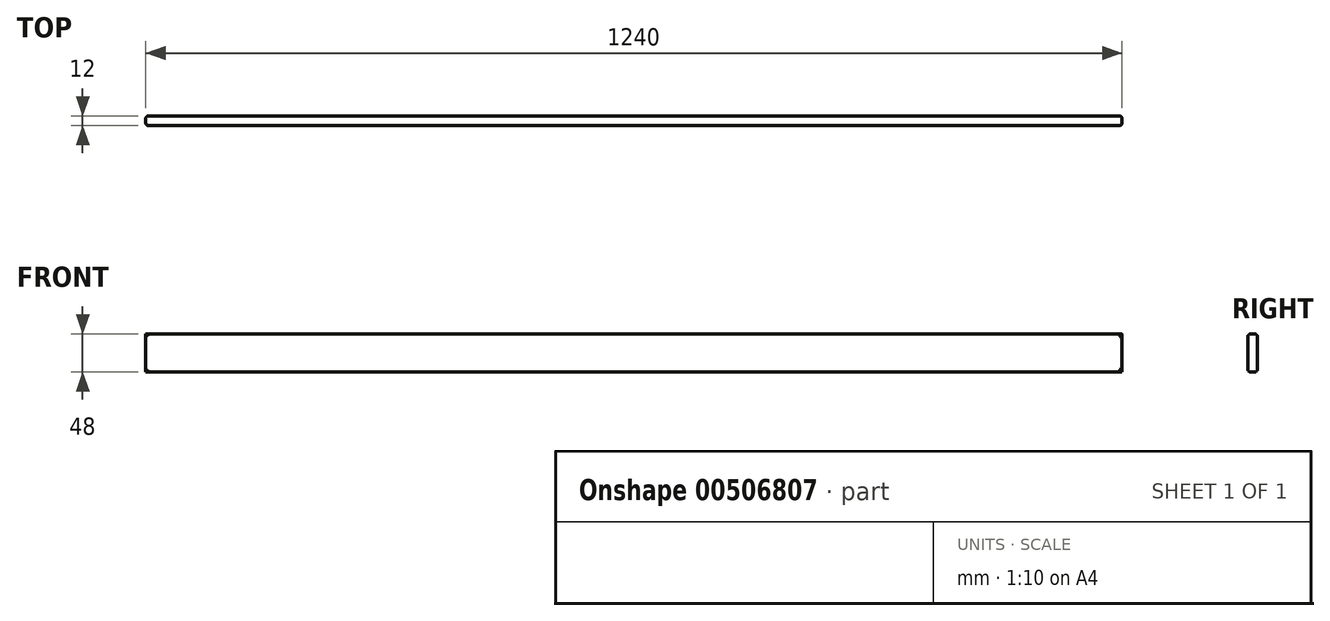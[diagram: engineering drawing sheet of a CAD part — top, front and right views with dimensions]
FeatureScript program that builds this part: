
annotation { "Feature Type Name" : "Feature", "Feature Type Description" : "" }
export const myFeature = defineFeature(function(context is Context, id is Id, definition is map)
    precondition{}
    {
        {
            var Q0;
            Q0=qCreatedBy(makeId("Front.planeOp"),FACE);
            var sketch = newSketch(context, id + "F0", { "sketchPlane" : qUnion([Q0])});
            skLineSegment(sketch, "E0.bottom", {"start": v(-617.25, 7.76) * mm, "end": v(622.75, 7.76) * mm});
            skLineSegment(sketch, "E0.top", {"start": v(-617.25, -40.24) * mm, "end": v(622.75, -40.24) * mm});
            skLineSegment(sketch, "E0.left", {"start": v(-617.25, 7.76) * mm, "end": v(-617.25, -40.24) * mm});
            skLineSegment(sketch, "E0.right", {"start": v(622.75, 7.76) * mm, "end": v(622.75, -40.24) * mm});
            skSolve(sketch);
        }
        {
            var Q0;
            Q0=makeQuery(id+"F0.imprint","IMPRINT",FACE,{"disambiguationData":[TD([[makeQuery(id+"F0.imprint","IMPRINT",EDGE,{"derivedFrom":sQuery(id+"F0.wireOp",EDGE,"E0.bottom")}),-1.0]])]});
            extrude(context, id + "F1", {"entities" : qUnion([Q0]), "depth" : 12 * mm});
        }
        {
            var Q0;
            Q0=makeQuery(id+"F1.opExtrude","CAP_FACE",FACE,{"disambiguationData":[OSD([sQuery(id+"F0.wireOp",EDGE,"E0.bottom"),sQuery(id+"F0.wireOp",EDGE,"E0.top"),sQuery(id+"F0.wireOp",EDGE,"E0.left"),sQuery(id+"F0.wireOp",EDGE,"E0.right")])],"isStart":false});
            var sketch = newSketch(context, id + "F2", { "sketchPlane" : qUnion([Q0])});
            skLineSegment(sketch, "E1", {"start": v(-617.25, 7.76) * mm, "end": v(-617.25, -12.24) * mm});
            skLineSegment(sketch, "E2", {"start": v(-617.25, -12.24) * mm, "end": v(622.75, -12.24) * mm});
            skPoint(sketch, "E3", {"position": v(2.75, -12.24) * mm});
            skSolve(sketch);
        }
        {
            var Q0;
            Q0=makeQuery(id+"F1.opExtrude","CAP_FACE",FACE,{"disambiguationData":[OSD([sQuery(id+"F0.wireOp",EDGE,"E0.bottom"),sQuery(id+"F0.wireOp",EDGE,"E0.top"),sQuery(id+"F0.wireOp",EDGE,"E0.left"),sQuery(id+"F0.wireOp",EDGE,"E0.right")])],"isStart":false});
            var Q1;
            Q1=makeQuery(id+"F1.opExtrude","CAP_FACE",FACE,{"disambiguationData":[OSD([sQuery(id+"F0.wireOp",EDGE,"E0.bottom"),sQuery(id+"F0.wireOp",EDGE,"E0.top"),sQuery(id+"F0.wireOp",EDGE,"E0.left"),sQuery(id+"F0.wireOp",EDGE,"E0.right")])],"isStart":true});
            fillet(context, id + "F3", {"entities" : qUnion([Q0, Q1]), "radius" : 3 * mm, "tangentPropagation" : true, "allowEdgeOverflow" : false});
        }
    });
